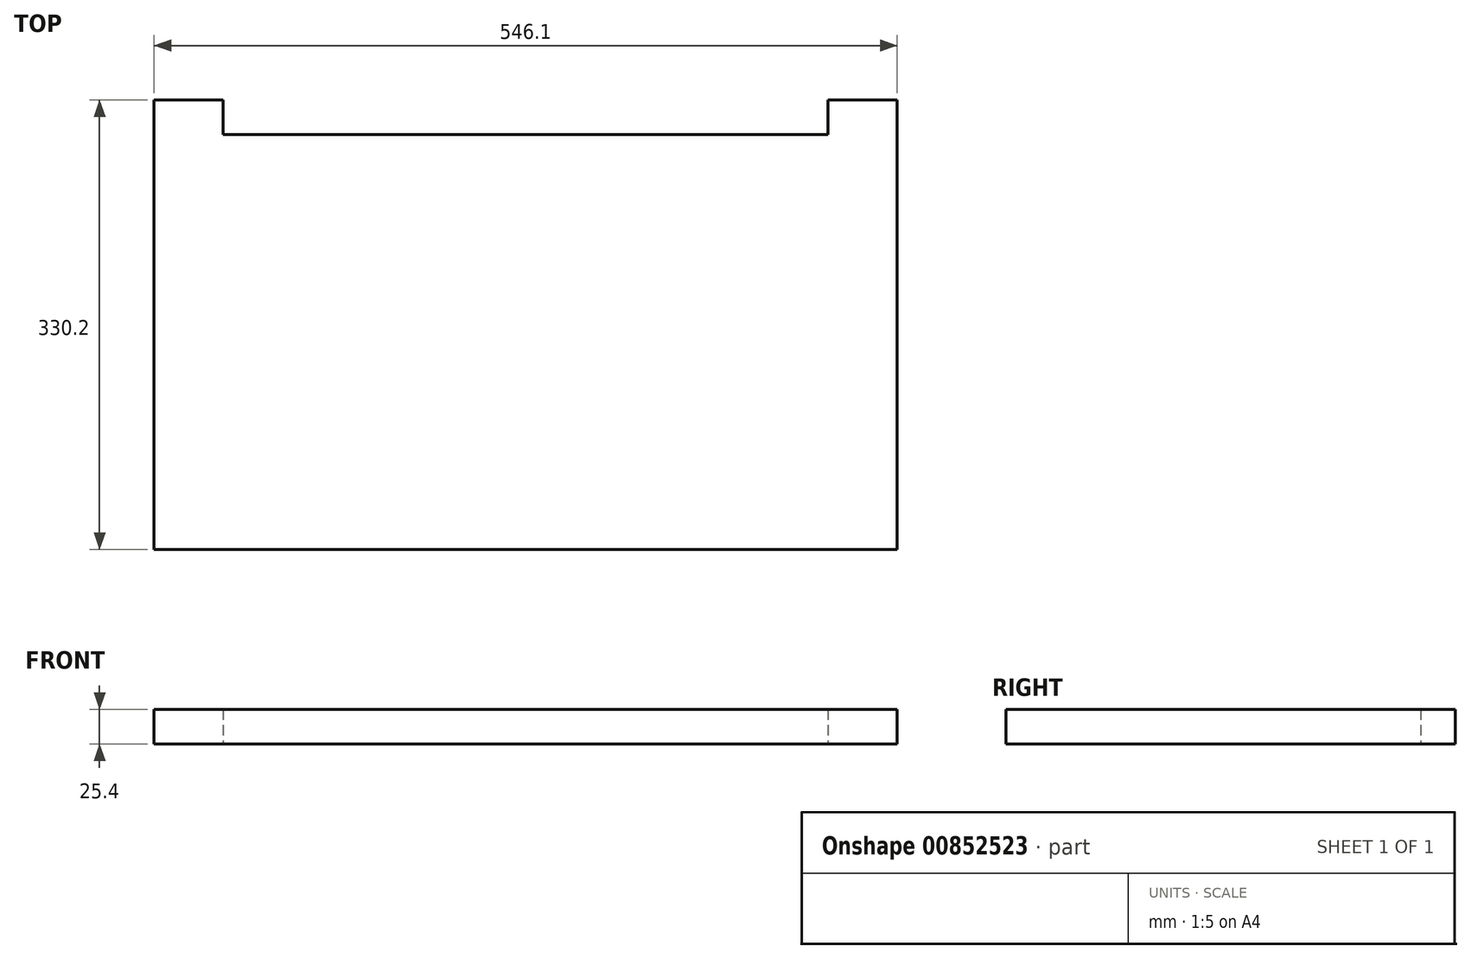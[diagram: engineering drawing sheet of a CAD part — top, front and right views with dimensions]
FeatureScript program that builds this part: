
annotation { "Feature Type Name" : "Feature", "Feature Type Description" : "" }
export const myFeature = defineFeature(function(context is Context, id is Id, definition is map)
    precondition{}
    {
        {
            var Q0;
            Q0=qCreatedBy(makeId("Top.planeOp"),FACE);
            var sketch = newSketch(context, id + "F0", { "sketchPlane" : qUnion([Q0])});
            skLineSegment(sketch, "E0.bottom", {"start": v(273.05, -165.1) * mm, "end": v(-273.05, -165.1) * mm});
            skLineSegment(sketch, "E0.top", {"start": v(273.05, 165.1) * mm, "end": v(222.25, 165.1) * mm});
            skLineSegment(sketch, "E0.left", {"start": v(273.05, -165.1) * mm, "end": v(273.05, 165.1) * mm});
            skLineSegment(sketch, "E0.right", {"start": v(-273.05, -165.1) * mm, "end": v(-273.05, 165.1) * mm});
            skPoint(sketch, "E0.middle", {"position": v(0, 0) * mm});
            skLineSegment(sketch, "E1.top", {"start": v(-222.25, 139.7) * mm, "end": v(222.25, 139.7) * mm});
            skLineSegment(sketch, "E1.left", {"start": v(-222.25, 165.1) * mm, "end": v(-222.25, 139.7) * mm});
            skLineSegment(sketch, "E1.right", {"start": v(222.25, 165.1) * mm, "end": v(222.25, 139.7) * mm});
            skLineSegment(sketch, "E2.trimOffspring", {"start": v(-222.25, 165.1) * mm, "end": v(-273.05, 165.1) * mm});
            skSolve(sketch);
        }
        {
            var Q0;
            Q0=qSketchRegion(id+"F0",true);
            extrude(context, id + "F1", {"entities" : qUnion([Q0]), "depth" : 25.4 * mm, "offsetDistance" : 25.4 * mm});
        }
    });
